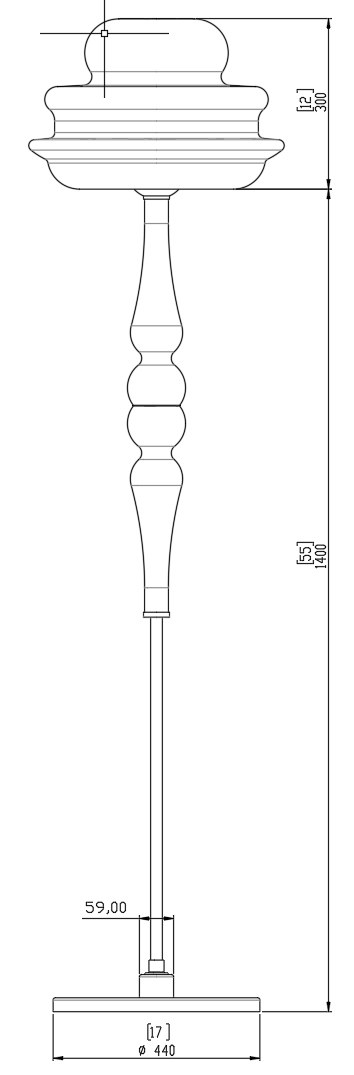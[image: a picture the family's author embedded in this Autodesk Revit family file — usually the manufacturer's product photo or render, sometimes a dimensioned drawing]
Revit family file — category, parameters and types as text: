
# Revit family: NOVECENTO-Floor
name_source: partatom
category: Lighting Fixtures
units: mm (PartAtom-declared; Revit-internal decimal feet)

## family parameters
Always vertical = Yes
Cut with Voids When Loaded = No
Light Source = No
OmniClass Number = 23.80.70.00
OmniClass Title = Lighting
Part Type = Normal
Room Calculation Point = No
Round Connector Dimension = Use Diameter
Shared = No
Work Plane-Based = Yes

## types (1)
- NOVECENTO PT
    Bulb Diametr = 15 mm  [stored 0.0492126 ft]
    Country = Europe
    Default Elevation = 1219 mm
    Depth = 0 mm  [stored 0 ft]
    Description = FLOOR LAMP
    Designer = Studio Debonademeo
    Manufacturer = Vistosi
    Manufacturer country = Italy
    Model = NOVECENTO
    Type Comments = Studio Debonademeo
    URL = https://vistosi.com
    URL Product Page = https://vistosi.it
    Width = 64 mm

note: [stored X ft] marks values corroborated as IEEE doubles in the binary element streams (Revit-internal decimal feet)

## geometry (parser evidence)
native form markers: Sweep x10
no freeform markers — native parametric forms only
